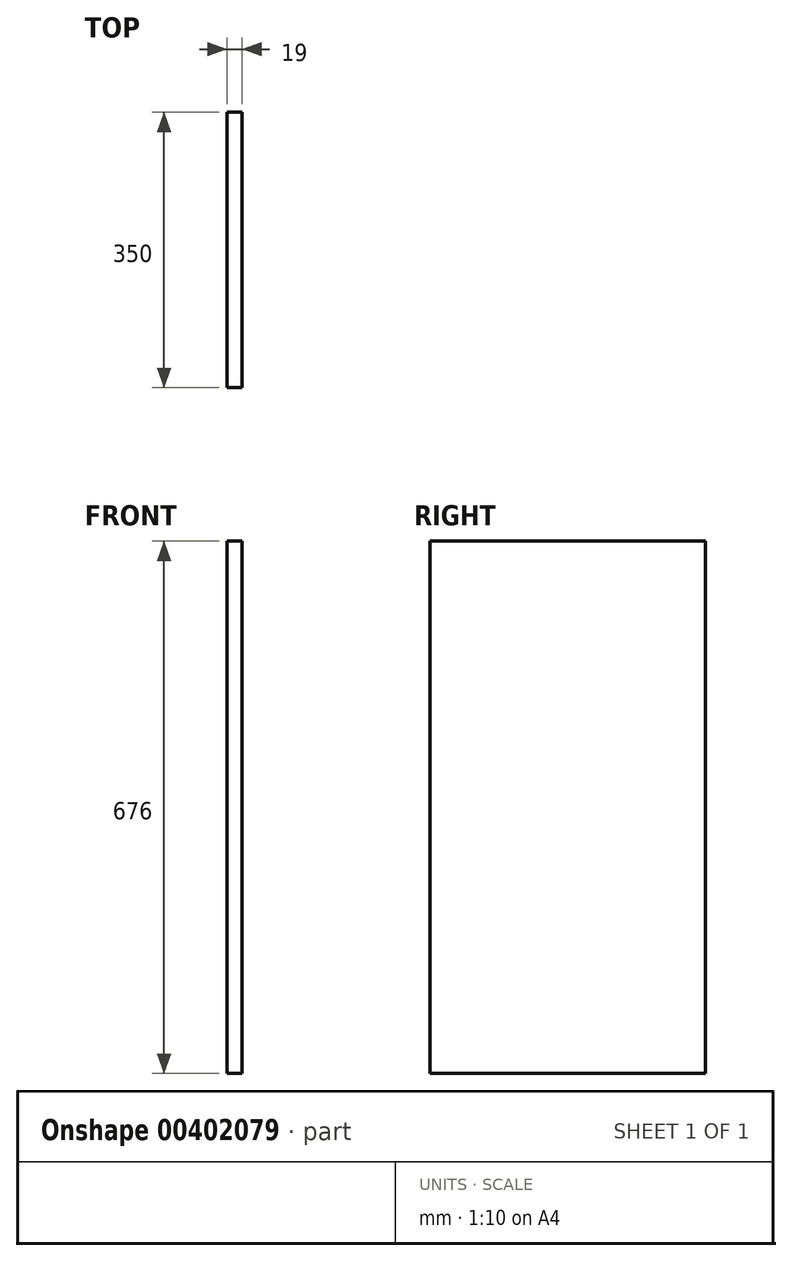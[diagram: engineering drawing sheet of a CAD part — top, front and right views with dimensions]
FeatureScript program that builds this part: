
annotation { "Feature Type Name" : "Feature", "Feature Type Description" : "" }
export const myFeature = defineFeature(function(context is Context, id is Id, definition is map)
    precondition{}
    {
        {
            var Q0;
            Q0=qCreatedBy(makeId("Right.planeOp"),FACE);
            var sketch = newSketch(context, id + "F0", { "sketchPlane" : qUnion([Q0])});
            skLineSegment(sketch, "E0.bottom", {"start": v(0, 0) * mm, "end": v(350, 0) * mm});
            skLineSegment(sketch, "E0.top", {"start": v(0, 676) * mm, "end": v(350, 676) * mm});
            skLineSegment(sketch, "E0.left", {"start": v(0, 0) * mm, "end": v(0, 676) * mm});
            skLineSegment(sketch, "E0.right", {"start": v(350, 0) * mm, "end": v(350, 676) * mm});
            skSolve(sketch);
        }
        {
            var Q0;
            Q0 = qSketchRegion(id + "F0", true);
            extrude(context, id + "F1", {"entities" : qUnion([Q0]), "depth" : 19 * mm});
        }
    });
